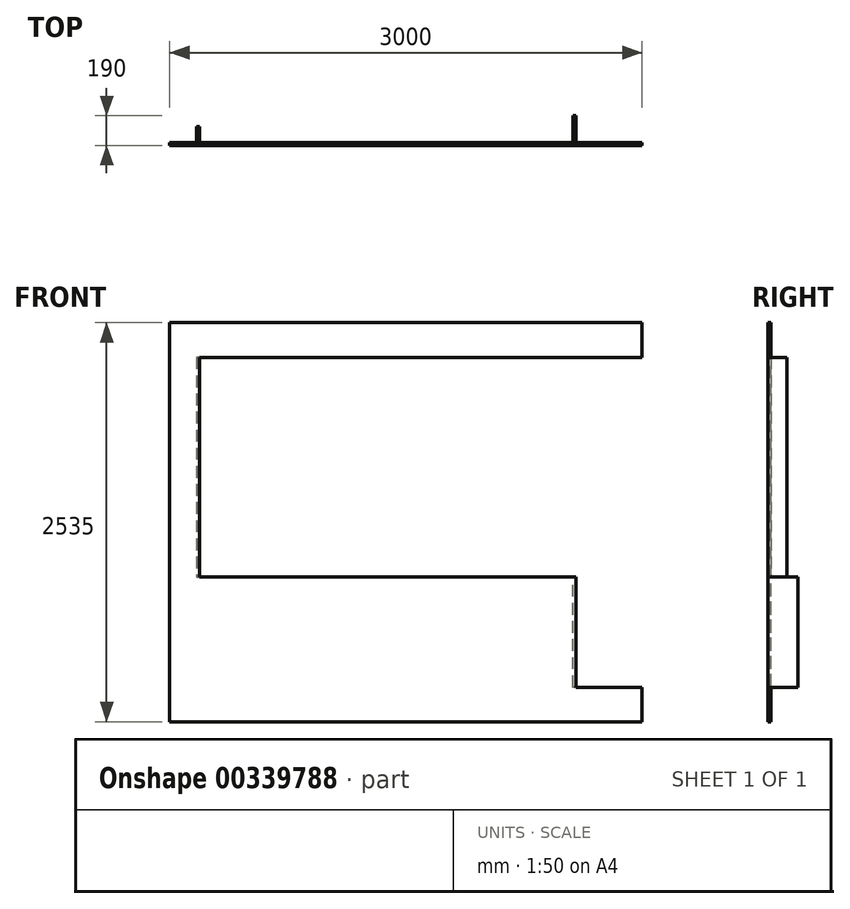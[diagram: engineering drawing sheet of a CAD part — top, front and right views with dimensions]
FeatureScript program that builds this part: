
annotation { "Feature Type Name" : "Feature", "Feature Type Description" : "" }
export const myFeature = defineFeature(function(context is Context, id is Id, definition is map)
    precondition{}
    {
        {
            var Q0;
            Q0=qCreatedBy(makeId("Front.planeOp"),FACE);
            var sketch = newSketch(context, id + "F0", { "sketchPlane" : qUnion([Q0])});
            skLineSegment(sketch, "E0.bottom", {"start": v(0, 0) * mm, "end": v(2560, 0) * mm});
            skLineSegment(sketch, "E0.top", {"start": v(170, 920) * mm, "end": v(2560, 920) * mm});
            skLineSegment(sketch, "E0.left", {"start": v(0, 0) * mm, "end": v(0, 920) * mm});
            skLineSegment(sketch, "E0.right", {"start": v(2560, 220) * mm, "end": v(2560, 920) * mm});
            skLineSegment(sketch, "E1", {"start": v(2560, 0) * mm, "end": v(3000, 0) * mm});
            skLineSegment(sketch, "E2", {"start": v(3000, 0) * mm, "end": v(3000, 220) * mm});
            skLineSegment(sketch, "E3", {"start": v(3000, 220) * mm, "end": v(2560, 220) * mm});
            skLineSegment(sketch, "E4", {"start": v(0, 920) * mm, "end": v(0, 2320) * mm});
            skLineSegment(sketch, "E5", {"start": v(0, 2320) * mm, "end": v(0, 2535) * mm});
            skLineSegment(sketch, "E6", {"start": v(0, 2535) * mm, "end": v(3000, 2535) * mm});
            skLineSegment(sketch, "E7", {"start": v(3000, 2535) * mm, "end": v(3000, 2315) * mm});
            skLineSegment(sketch, "E8", {"start": v(3000, 2315) * mm, "end": v(170, 2315) * mm});
            skLineSegment(sketch, "E9", {"start": v(170, 2315) * mm, "end": v(170, 920) * mm});
            skSolve(sketch);
        }
        {
            var Q0;
            Q0=makeQuery(id+"F0.imprint","IMPRINT",FACE,{"disambiguationData":[TD([[makeQuery(id+"F0.imprint","IMPRINT",EDGE,{"derivedFrom":sQuery(id+"F0.wireOp",EDGE,"E0.bottom")}),1.0]])]});
            extrude(context, id + "F1", {"entities" : qUnion([Q0]), "depth" : 20 * mm});
        }
        {
            var Q0;
            Q0=makeQuery(id+"F1.opExtrude","SWEPT_FACE",FACE,{"disambiguationData":[OSD([sQuery(id+"F0.wireOp",EDGE,"E0.right")])]});
            var sketch = newSketch(context, id + "F2", { "sketchPlane" : qUnion([Q0])});
            skLineSegment(sketch, "E10.0", {"start": v(170, 220) * mm, "end": v(170, 920) * mm});
            skLineSegment(sketch, "E11", {"start": v(-20, 920) * mm, "end": v(170, 920) * mm});
            skLineSegment(sketch, "E12", {"start": v(-20, 220) * mm, "end": v(170, 220) * mm});
            skLineSegment(sketch, "E13", {"start": v(-20, 920) * mm, "end": v(-20, 220) * mm});
            skSolve(sketch);
        }
        {
            var Q0;
            Q0 = qSketchRegion(id + "F2", true);
            extrude(context, id + "F3", {"entities" : qUnion([Q0]), "operationType" : NewBodyOperationType.ADD, "depth" : 20 * mm});
        }
        {
            var Q0;
            Q0=makeQuery(id+"F1.opExtrude","SWEPT_FACE",FACE,{"disambiguationData":[OSD([sQuery(id+"F0.wireOp",EDGE,"E9")])]});
            var sketch = newSketch(context, id + "F4", { "sketchPlane" : qUnion([Q0])});
            skLineSegment(sketch, "E14.0", {"start": v(100, 2315) * mm, "end": v(100, 920) * mm});
            skLineSegment(sketch, "E15", {"start": v(-20, 2315) * mm, "end": v(100, 2315) * mm});
            skLineSegment(sketch, "E16", {"start": v(-20, 920) * mm, "end": v(100, 920) * mm});
            skLineSegment(sketch, "E17", {"start": v(-20, 2315) * mm, "end": v(-20, 920) * mm});
            skSolve(sketch);
        }
        {
            var Q0;
            Q0 = qSketchRegion(id + "F4", true);
            extrude(context, id + "F5", {"entities" : qUnion([Q0]), "operationType" : NewBodyOperationType.ADD, "depth" : 20 * mm});
        }
    });
